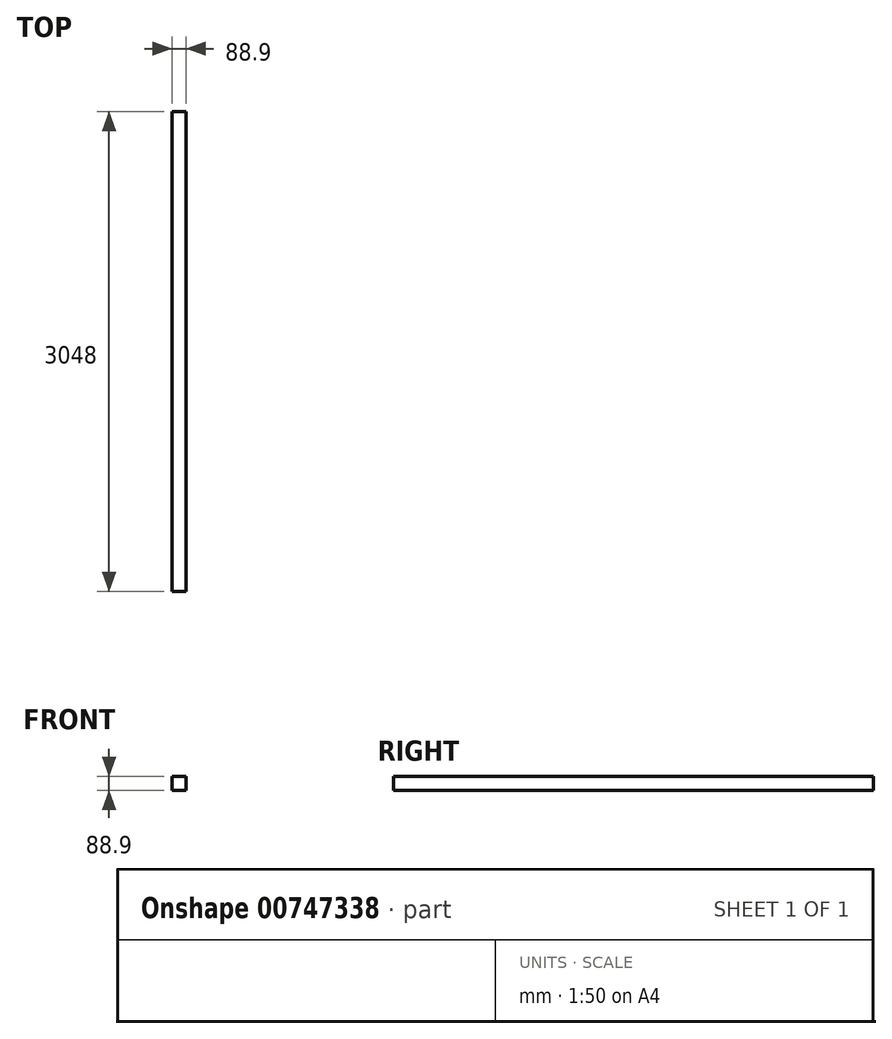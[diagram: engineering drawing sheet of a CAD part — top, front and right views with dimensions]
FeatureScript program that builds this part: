
annotation { "Feature Type Name" : "Feature", "Feature Type Description" : "" }
export const myFeature = defineFeature(function(context is Context, id is Id, definition is map)
    precondition{}
    {
        {
            var Q0;
            Q0=qCreatedBy(makeId("Front.planeOp"),FACE);
            var sketch = newSketch(context, id + "F0", { "sketchPlane" : qUnion([Q0])});
            skLineSegment(sketch, "E0.bottom", {"start": v(0, 0) * mm, "end": v(88.9, 0) * mm});
            skLineSegment(sketch, "E0.top", {"start": v(0, 88.9) * mm, "end": v(88.9, 88.9) * mm});
            skLineSegment(sketch, "E0.left", {"start": v(0, 0) * mm, "end": v(0, 88.9) * mm});
            skLineSegment(sketch, "E0.right", {"start": v(88.9, 0) * mm, "end": v(88.9, 88.9) * mm});
            skSolve(sketch);
        }
        {
            var Q0;
            Q0=makeQuery(id+"F0.imprint","IMPRINT",FACE,{"disambiguationData":[TD([[makeQuery(id+"F0.imprint","IMPRINT",EDGE,{"derivedFrom":sQuery(id+"F0.wireOp",EDGE,"E0.bottom")}),1.0]])]});
            extrude(context, id + "F1", {"entities" : qUnion([Q0]), "depth" : 3048 * mm, "offsetDistance" : 25.4 * mm});
        }
    });
